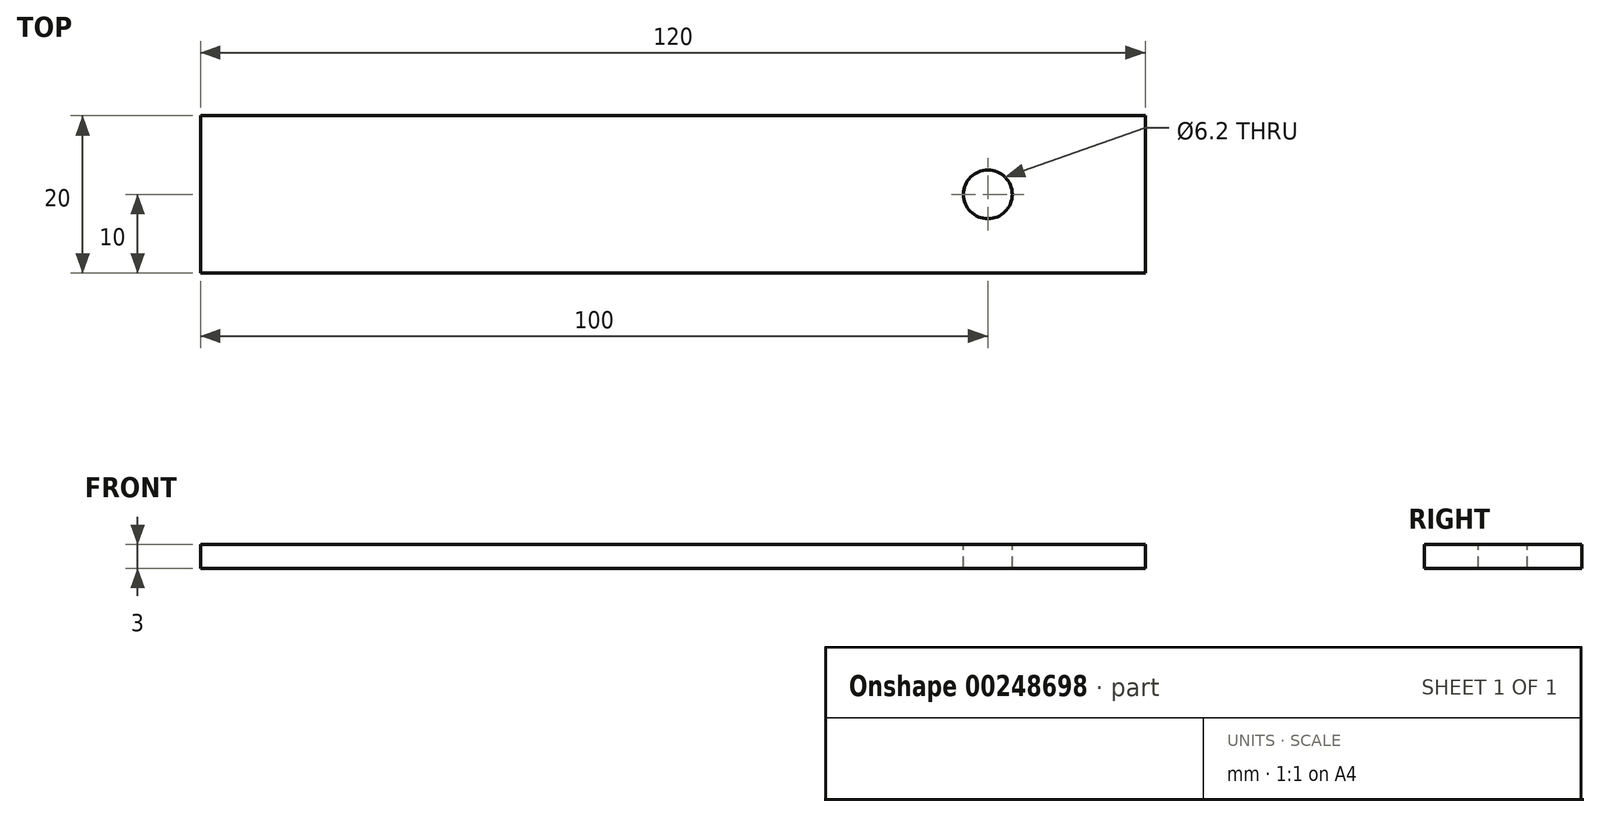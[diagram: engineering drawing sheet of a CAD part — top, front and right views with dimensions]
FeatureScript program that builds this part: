
annotation { "Feature Type Name" : "Feature", "Feature Type Description" : "" }
export const myFeature = defineFeature(function(context is Context, id is Id, definition is map)
    precondition{}
    {
        {
            var Q0;
            Q0=qCreatedBy(makeId("Top.planeOp"),FACE);
            var sketch = newSketch(context, id + "F0", { "sketchPlane" : qUnion([Q0])});
            skLineSegment(sketch, "E0.bottom", {"start": v(60, -10) * mm, "end": v(-60, -10) * mm});
            skLineSegment(sketch, "E0.top", {"start": v(60, 10) * mm, "end": v(-60, 10) * mm});
            skLineSegment(sketch, "E0.left", {"start": v(60, -10) * mm, "end": v(60, 10) * mm});
            skLineSegment(sketch, "E0.right", {"start": v(-60, -10) * mm, "end": v(-60, 10) * mm});
            skPoint(sketch, "E0.middle", {"position": v(0, 0) * mm});
            skSolve(sketch);
        }
        {
            var Q0;
            Q0 = qSketchRegion(id + "F0", true);
            extrude(context, id + "F1", {"entities" : qUnion([Q0]), "depth" : 3 * mm});
        }
        {
            var Q0;
            Q0=makeQuery(id+"F1.opExtrude","CAP_FACE",FACE,{"disambiguationData":[OSD([sQuery(id+"F0.wireOp",EDGE,"E0.bottom"),sQuery(id+"F0.wireOp",EDGE,"E0.top"),sQuery(id+"F0.wireOp",EDGE,"E0.left"),sQuery(id+"F0.wireOp",EDGE,"E0.right")])],"isStart":false});
            var sketch = newSketch(context, id + "F2", { "sketchPlane" : qUnion([Q0])});
            skCircle(sketch, "E1", {"center": v(40, 0) * mm, "radius": 3.1 * mm});
            skPoint(sketch, "E1.centerSnap0", {"position": v(60, 0) * mm});
            skSolve(sketch);
        }
        {
            var Q0;
            Q0 = qSketchRegion(id + "F2", true);
            extrude(context, id + "F3", {"entities" : qUnion([Q0]), "operationType" : NewBodyOperationType.REMOVE, "oppositeDirection" : true, "depth" : 25 * mm});
        }
    });
